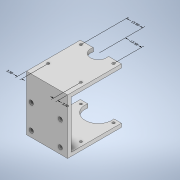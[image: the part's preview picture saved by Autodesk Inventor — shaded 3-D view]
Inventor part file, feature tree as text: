
AUTODESK INVENTOR PART (.ipt)
format: ipt  version: 2022 (Build 260153000, 153)  size: 175,104 bytes
history: native  units: mm
features: sketch x6, other x5, extrude x4, hole x2
ambient origin geometry x8: Origin, YZ Plane, XZ Plane, XY Plane, X Axis, Y Axis, Z Axis, Center Point
bodies: Body1 (feature_tree)
feature tree (17):
  other  "ソリッド1"
  extrude  "押し出し1"  Depth=44.5mm
  extrude  "押し出し2"  Depth=34.0mm
  extrude  "押し出し3"  Depth=45.5mm TaperAngle=0.0deg
  extrude  "押し出し4"  Depth=3.0mm
  hole  "穴1"  [1 undecoded]
  hole  "穴2"  [1 undecoded]
  sketch  "スケッチ1"
  sketch  "スケッチ2"
  sketch  "スケッチ3"
  sketch  "スケッチ4"
  sketch  "スケッチ5"
  sketch  "スケッチ6"
  other  "長さ寸法 1"
  other  "長さ寸法 2"
  other  "長さ寸法 3"
  other  "長さ寸法 4"
note: 2 required parameter values undecoded (feature->parameter linkage not recoverable at this tier; creation-order binding heuristic only, values carry confidence <= 0.55)
